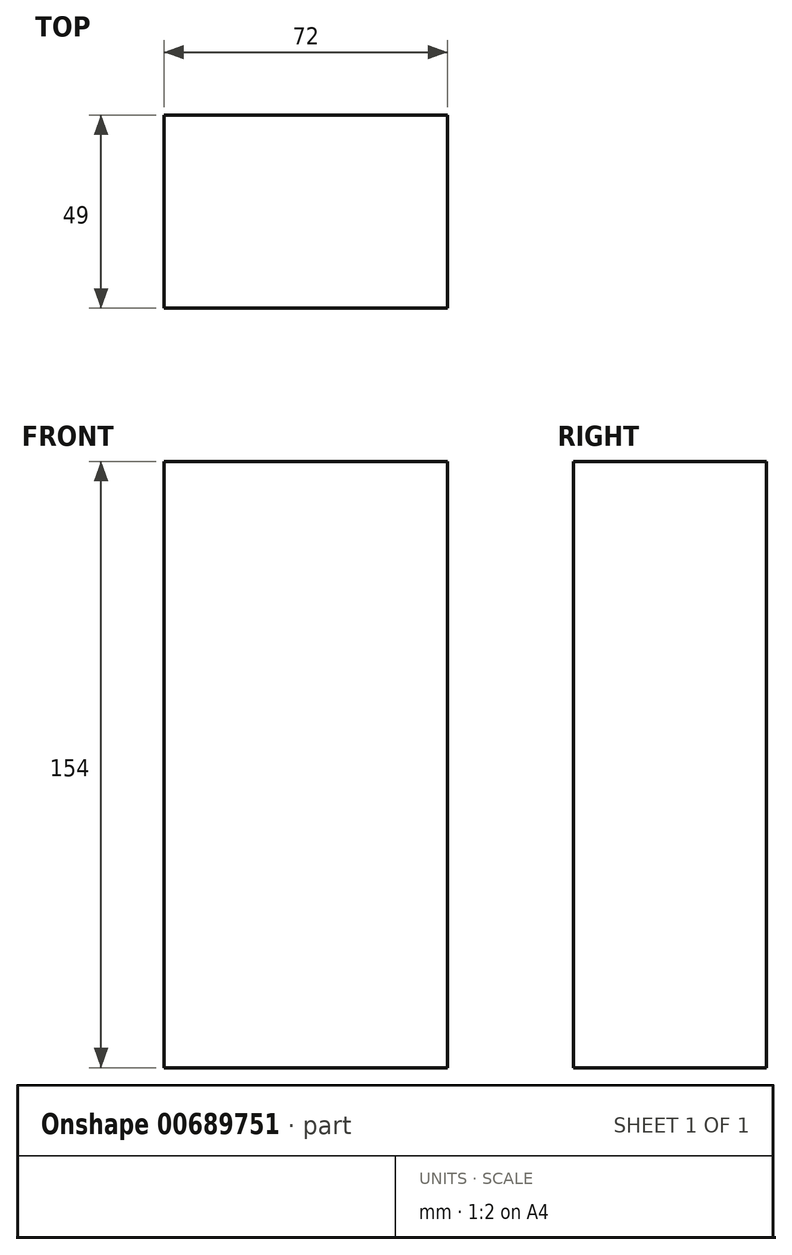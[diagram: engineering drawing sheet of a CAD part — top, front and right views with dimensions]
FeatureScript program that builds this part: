
annotation { "Feature Type Name" : "Feature", "Feature Type Description" : "" }
export const myFeature = defineFeature(function(context is Context, id is Id, definition is map)
    precondition{}
    {
        {
            var Q0;
            Q0=qCreatedBy(makeId("Front.planeOp"),FACE);
            var sketch = newSketch(context, id + "F0", { "sketchPlane" : qUnion([Q0])});
            skLineSegment(sketch, "E0.bottom", {"start": v(36, 77) * mm, "end": v(-36, 77) * mm});
            skLineSegment(sketch, "E0.top", {"start": v(36, -77) * mm, "end": v(-36, -77) * mm});
            skLineSegment(sketch, "E0.left", {"start": v(36, 77) * mm, "end": v(36, -77) * mm});
            skLineSegment(sketch, "E0.right", {"start": v(-36, 77) * mm, "end": v(-36, -77) * mm});
            skPoint(sketch, "E0.middle", {"position": v(0, 0) * mm});
            skSolve(sketch);
        }
        {
            var Q0;
            Q0=makeQuery(id+"F0.imprint","IMPRINT",FACE,{"disambiguationData":[TD([[makeQuery(id+"F0.imprint","IMPRINT",EDGE,{"derivedFrom":sQuery(id+"F0.wireOp",EDGE,"E0.bottom")}),1.0]])]});
            extrude(context, id + "F1", {"entities" : qUnion([Q0]), "depth" : 49 * mm, "offsetDistance" : 25.4 * mm});
        }
    });
